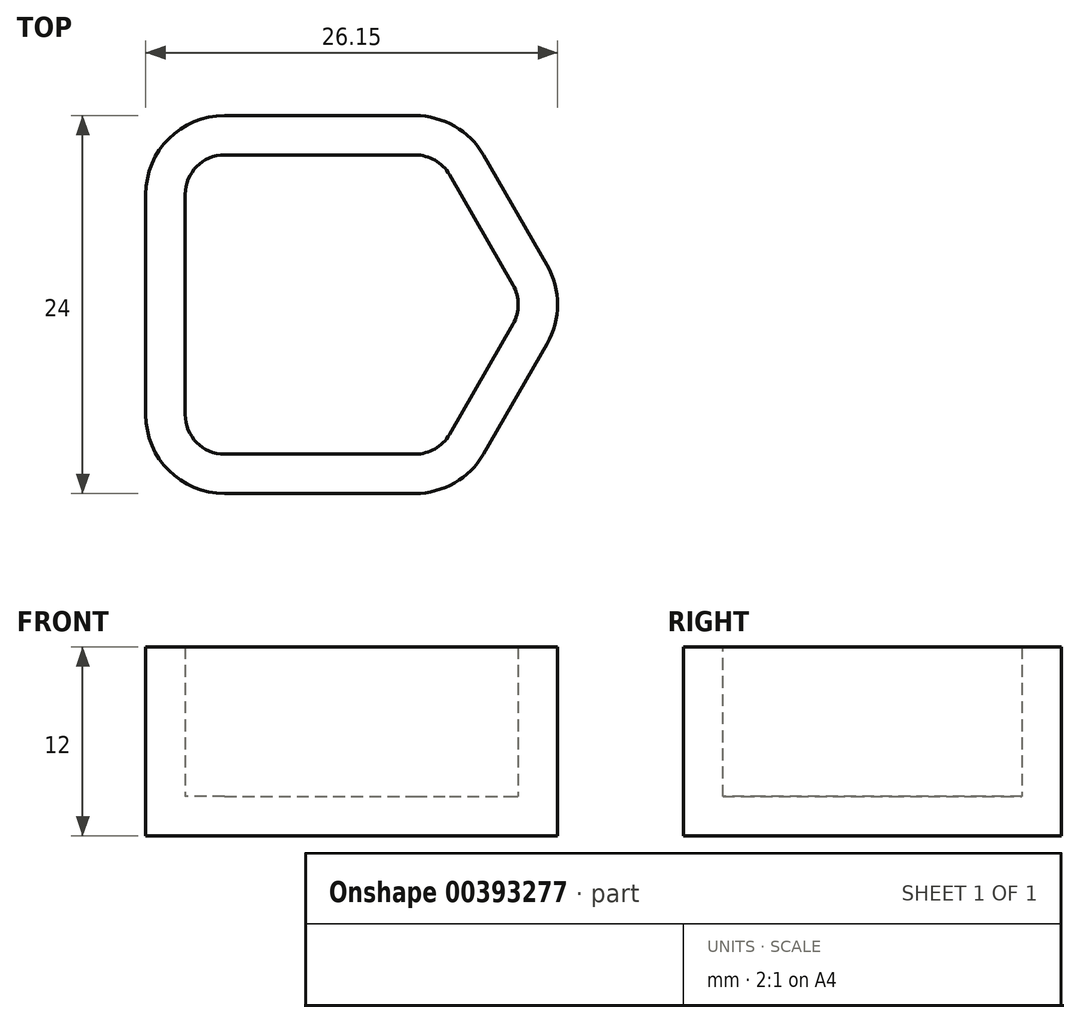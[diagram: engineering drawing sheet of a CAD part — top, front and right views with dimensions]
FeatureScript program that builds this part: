
annotation { "Feature Type Name" : "Feature", "Feature Type Description" : "" }
export const myFeature = defineFeature(function(context is Context, id is Id, definition is map)
    precondition{}
    {
        {
            var Q0;
            Q0=qCreatedBy(makeId("Top.planeOp"),FACE);
            var sketch = newSketch(context, id + "F0", { "sketchPlane" : qUnion([Q0])});
            skLineSegment(sketch, "E0", {"start": v(0, 7) * mm, "end": v(0, 0) * mm});
            skLineSegment(sketch, "E1", {"start": v(0, 0) * mm, "end": v(0, -7) * mm});
            skLineSegment(sketch, "E2", {"start": v(5, -12) * mm, "end": v(17.11, -12) * mm});
            skLineSegment(sketch, "E3", {"start": v(21.44, -9.5) * mm, "end": v(25.48, -2.5) * mm});
            skLineSegment(sketch, "E4", {"start": v(25.48, 2.5) * mm, "end": v(21.44, 9.5) * mm});
            skLineSegment(sketch, "E5", {"start": v(17.11, 12) * mm, "end": v(5, 12) * mm});
            skPoint(sketch, "E6.visualSharp", {"position": v(20, 12) * mm});
            skArc(sketch, "E6.filletArc", {"start": v(21.44, 9.5) * mm, "mid": v(19.61, 11.33) * mm, "end": v(17.11, 12) * mm});
            skPoint(sketch, "E7.visualSharp", {"position": v(20, -12) * mm});
            skArc(sketch, "E7.filletArc", {"start": v(17.11, -12) * mm, "mid": v(19.61, -11.33) * mm, "end": v(21.44, -9.5) * mm});
            skPoint(sketch, "E8.visualSharp", {"position": v(0, 12) * mm});
            skArc(sketch, "E8.filletArc", {"start": v(5, 12) * mm, "mid": v(1.46, 10.54) * mm, "end": v(0, 7) * mm});
            skPoint(sketch, "E9.visualSharp", {"position": v(0, -12) * mm});
            skArc(sketch, "E9.filletArc", {"start": v(0, -7) * mm, "mid": v(1.46, -10.54) * mm, "end": v(5, -12) * mm});
            skPoint(sketch, "E10.visualSharp", {"position": v(26.93, 0) * mm});
            skArc(sketch, "E10.filletArc", {"start": v(25.48, -2.5) * mm, "mid": v(26.15, 0) * mm, "end": v(25.48, 2.5) * mm});
            skSolve(sketch);
        }
        {
            var Q0;
            Q0 = qSketchRegion(id + "F0", true);
            extrude(context, id + "F1", {"entities" : qUnion([Q0]), "depth" : 12 * mm});
        }
        {
            var Q0;
            Q0=makeQuery(id+"F1.opExtrude","CAP_FACE",FACE,{"disambiguationData":[OSD([sQuery(id+"F0.wireOp",EDGE,"E0"),sQuery(id+"F0.wireOp",EDGE,"E1"),sQuery(id+"F0.wireOp",EDGE,"E2"),sQuery(id+"F0.wireOp",EDGE,"E3"),sQuery(id+"F0.wireOp",EDGE,"E4"),sQuery(id+"F0.wireOp",EDGE,"E5"),sQuery(id+"F0.wireOp",EDGE,"E6.filletArc"),sQuery(id+"F0.wireOp",EDGE,"E7.filletArc"),sQuery(id+"F0.wireOp",EDGE,"E8.filletArc"),sQuery(id+"F0.wireOp",EDGE,"E9.filletArc"),sQuery(id+"F0.wireOp",EDGE,"E10.filletArc")])],"isStart":false});
            shell(context, id + "F2", {"entities" : qUnion([Q0]), "thickness" : 2.5 * mm});
        }
    });
